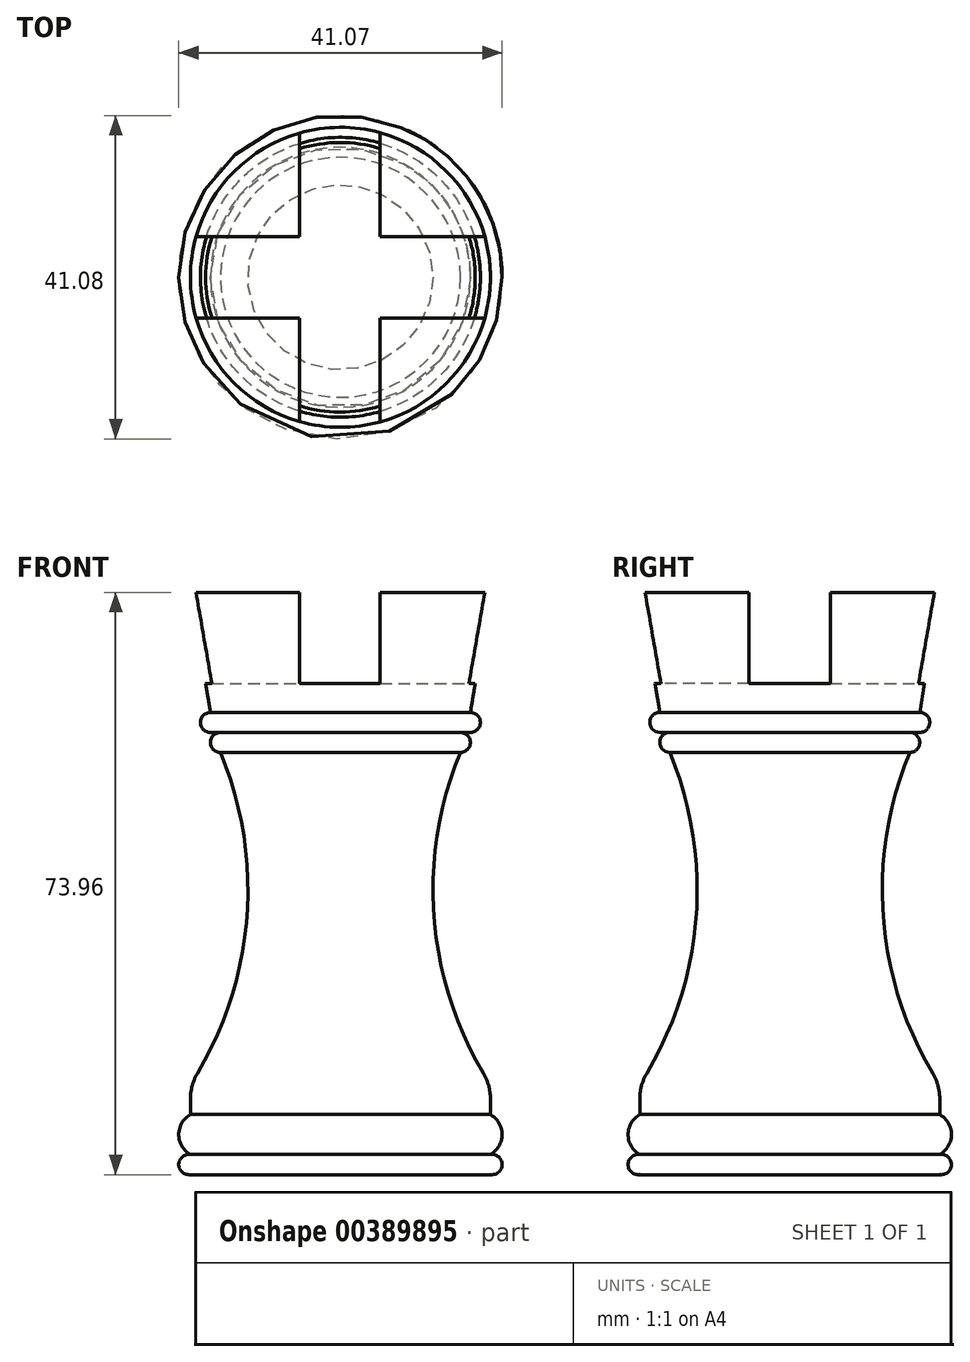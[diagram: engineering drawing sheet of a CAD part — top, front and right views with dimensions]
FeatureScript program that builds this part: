
annotation { "Feature Type Name" : "Feature", "Feature Type Description" : "" }
export const myFeature = defineFeature(function(context is Context, id is Id, definition is map)
    precondition{}
    {
        {
            var Q0;
            Q0=qCreatedBy(makeId("Front.planeOp"),FACE);
            var sketch = newSketch(context, id + "F0", { "sketchPlane" : qUnion([Q0])});
            skLineSegment(sketch, "E0", {"start": v(-58.9, -34.46) * mm, "end": v(-39.86, -34.46) * mm});
            skLineSegment(sketch, "E1", {"start": v(-58.9, -29.38) * mm, "end": v(-39.86, -29.38) * mm});
            skLineSegment(sketch, "E2", {"start": v(-39.86, -34.46) * mm, "end": v(-39.86, -29.38) * mm});
            skLineSegment(sketch, "E3", {"start": v(-58.9, -37) * mm, "end": v(-39.86, -37) * mm});
            skArc(sketch, "E4", {"start": v(-58.9, -34.46) * mm, "mid": v(-60.4, -35.73) * mm, "end": v(-58.9, -37) * mm});
            skArc(sketch, "E5", {"start": v(-58.9, -29.38) * mm, "mid": v(-60.4, -31.92) * mm, "end": v(-58.9, -34.46) * mm});
            skLineSegment(sketch, "E6", {"start": v(-56.37, 21.7) * mm, "end": v(-58.9, 36.94) * mm});
            skLineSegment(sketch, "E7", {"start": v(-39.86, 36.94) * mm, "end": v(-39.86, -37) * mm});
            skLineSegment(sketch, "E8", {"start": v(-58.9, 36.94) * mm, "end": v(-49.38, 36.94) * mm});
            skLineSegment(sketch, "E9", {"start": v(-39.86, 36.94) * mm, "end": v(-49.38, 36.94) * mm});
            skLineSegment(sketch, "E10", {"start": v(-56.37, 21.7) * mm, "end": v(-39.86, 21.7) * mm});
            skLineSegment(sketch, "E11", {"start": v(-56.37, 21.7) * mm, "end": v(-56.37, 19.16) * mm});
            skLineSegment(sketch, "E12", {"start": v(-56.37, 19.16) * mm, "end": v(-55.1, 19.16) * mm});
            skLineSegment(sketch, "E13", {"start": v(-55.1, 19.16) * mm, "end": v(-39.86, 19.16) * mm});
            skLineSegment(sketch, "E14", {"start": v(-55.1, 16.62) * mm, "end": v(-39.86, 16.62) * mm});
            skPoint(sketch, "E15", {"position": v(-56.37, 17.89) * mm});
            skArc(sketch, "E16", {"start": v(-55.1, 19.16) * mm, "mid": v(-56.37, 17.89) * mm, "end": v(-55.1, 16.62) * mm});
            skLineSegment(sketch, "E17", {"start": v(-56.37, 20.43) * mm, "end": v(-57.64, 20.43) * mm});
            skArc(sketch, "E18", {"start": v(-56.37, 21.7) * mm, "mid": v(-57.64, 20.43) * mm, "end": v(-56.37, 19.16) * mm});
            skLineSegment(sketch, "E19", {"start": v(-58.9, -29.38) * mm, "end": v(-58.9, -27.38) * mm});
            skArc(sketch, "E20", {"start": v(-58.01, -24.13) * mm, "mid": v(-51.73, -4.1) * mm, "end": v(-55.1, 16.62) * mm});
            skArc(sketch, "E21.filletArc", {"start": v(-58.01, -24.13) * mm, "mid": v(-58.68, -25.7) * mm, "end": v(-58.9, -27.38) * mm});
            skSolve(sketch);
        }
        {
            var Q0;
            Q0 = qSketchRegion(id + "F0", true);
            var Q1;
            Q1=sQuery(id+"F0.wireOp",EDGE,"E7");
            revolve(context, id + "F1", {"entities" : qUnion([Q0]), "axis" : qUnion([Q1]), "revolveType" : RevolveType.FULL});
        }
        {
            var Q0;
            Q0=qCreatedBy(makeId("Top.planeOp"),FACE);
            var sketch = newSketch(context, id + "F2", { "sketchPlane" : qUnion([Q0])});
            skLineSegment(sketch, "E22", {"start": v(-34.8, -5.16) * mm, "end": v(-19.38, -5.16) * mm});
            skLineSegment(sketch, "E23", {"start": v(-19.38, -5.16) * mm, "end": v(-19.38, 5.16) * mm});
            skLineSegment(sketch, "E24", {"start": v(-29.66, 5.16) * mm, "end": v(-19.38, 5.16) * mm});
            skLineSegment(sketch, "E25", {"start": v(-29.66, 5.16) * mm, "end": v(-34.8, 5.16) * mm});
            skLineSegment(sketch, "E26", {"start": v(-34.8, 5.16) * mm, "end": v(-34.8, 20.63) * mm});
            skLineSegment(sketch, "E27", {"start": v(-34.8, 20.63) * mm, "end": v(-39.94, 20.63) * mm});
            skLineSegment(sketch, "E28.MirrorCS", {"start": v(-45.08, 5.16) * mm, "end": v(-45.08, 20.63) * mm});
            skLineSegment(sketch, "E29.MirrorCS", {"start": v(-50.22, 5.16) * mm, "end": v(-45.08, 5.16) * mm});
            skLineSegment(sketch, "E30.MirrorCS", {"start": v(-50.22, 5.16) * mm, "end": v(-60.5, 5.16) * mm});
            skLineSegment(sketch, "E31.MirrorCS", {"start": v(-60.5, -5.16) * mm, "end": v(-60.5, 5.16) * mm});
            skLineSegment(sketch, "E32.MirrorCS", {"start": v(-45.08, -5.16) * mm, "end": v(-60.5, -5.16) * mm});
            skLineSegment(sketch, "E33.MirrorCS", {"start": v(-45.08, 20.63) * mm, "end": v(-39.94, 20.63) * mm});
            skLineSegment(sketch, "E34.MirrorCS", {"start": v(-45.08, -5.16) * mm, "end": v(-45.08, -20.63) * mm});
            skLineSegment(sketch, "E35.MirrorCS", {"start": v(-34.8, -5.16) * mm, "end": v(-34.8, -20.63) * mm});
            skLineSegment(sketch, "E36.MirrorCS", {"start": v(-34.8, -20.63) * mm, "end": v(-39.94, -20.63) * mm});
            skLineSegment(sketch, "E37.MirrorCS", {"start": v(-45.08, -20.63) * mm, "end": v(-39.94, -20.63) * mm});
            skSolve(sketch);
        }
        {
            var Q0;
            Q0 = qSketchRegion(id + "F2", true);
            extrude(context, id + "F3", {"entities" : qUnion([Q0]), "operationType" : NewBodyOperationType.REMOVE, "depth" : 50.8 * mm, "hasSecondDirection" : true, "secondDirectionOppositeDirection" : false, "secondDirectionDepth" : 25.4 * mm});
        }
    });
